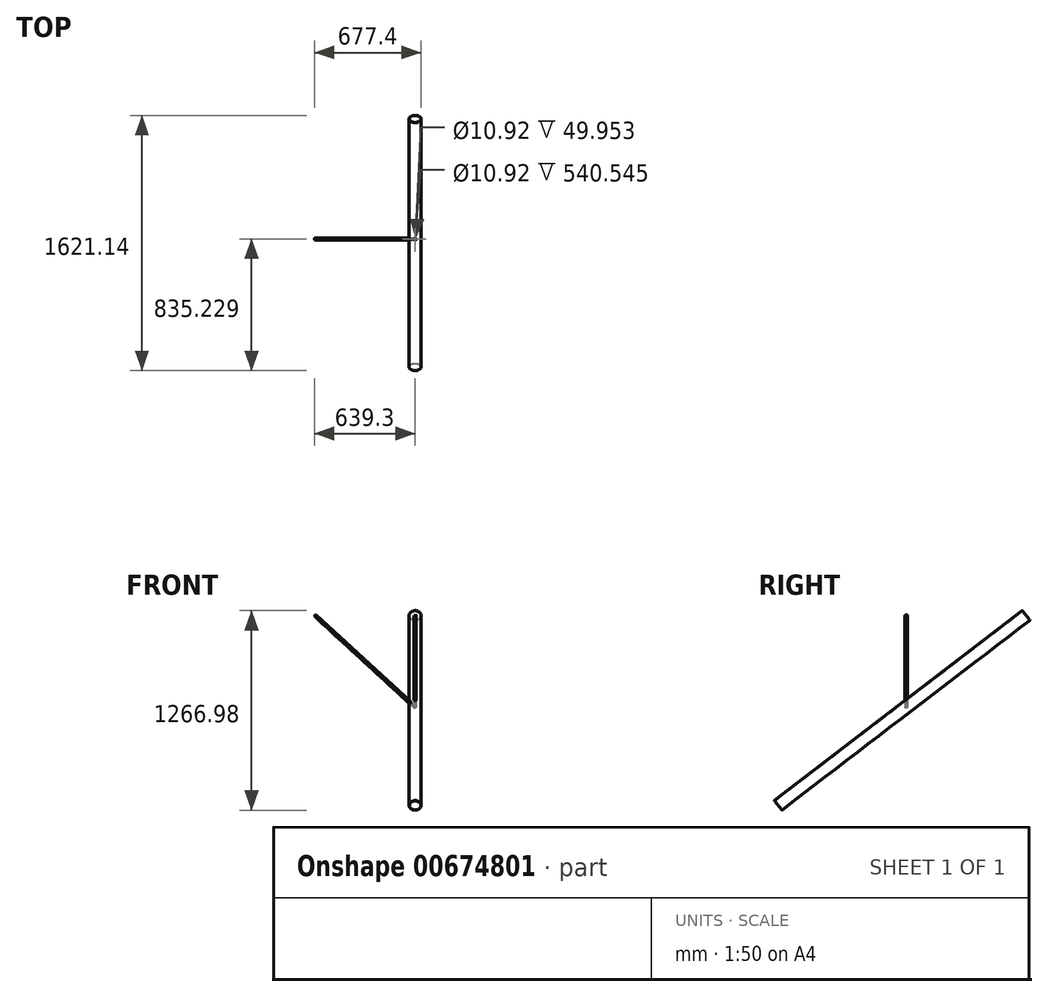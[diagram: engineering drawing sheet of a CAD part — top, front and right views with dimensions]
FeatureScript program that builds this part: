
annotation { "Feature Type Name" : "Feature", "Feature Type Description" : "" }
export const myFeature = defineFeature(function(context is Context, id is Id, definition is map)
    precondition{}
    {
        {
            var Q0;
            Q0=qCreatedBy(makeId("Right.planeOp"),FACE);
            var sketch = newSketch(context, id + "F0", { "sketchPlane" : qUnion([Q0])});
            skLineSegment(sketch, "E0", {"start": v(0, 0) * mm, "end": v(-1574.8, -1206.5) * mm});
            skSolve(sketch);
        }
        {
            var Q0;
            Q0=sQuery(id+"F0.wireOp",VERTEX,"E0.end");
            var Q1;
            Q1=sQuery(id+"F0.wireOp",EDGE,"E0");
            cPlane(context, id + "F1", {"entities" : qUnion([Q0, Q1]), "cplaneType" : CPlaneType.LINE_POINT, "offset" : 25.4 * mm, "width" : 152.4 * mm, "height" : 152.4 * mm});
        }
        {
            var Q0;
            Q0=qCreatedBy(id+"F1.planeOp",FACE);
            var sketch = newSketch(context, id + "F2", { "sketchPlane" : qUnion([Q0])});
            skCircle(sketch, "E1", {"center": v(0, 0) * mm, "radius": 38.1 * mm});
            skSolve(sketch);
        }
        {
            var Q0;
            Q0=makeQuery(id+"F2.imprint","IMPRINT",FACE,{"disambiguationData":[TD([[makeQuery(id+"F2.imprint","IMPRINT",EDGE,{"derivedFrom":sQuery(id+"F2.wireOp",EDGE,"E1")}),1.0]])]});
            var Q1;
            Q1=sQuery(id+"F0.wireOp",EDGE,"E0");
            sweep(context, id + "F3", {"profiles" : qUnion([Q0]), "path" : qUnion([Q1])});
        }
        {
            var Q0;
            Q0=qCreatedBy(id+"F1.planeOp",FACE);
            var sketch = newSketch(context, id + "F4", { "sketchPlane" : qUnion([Q0])});
            skCircle(sketch, "E2", {"center": v(0, 0) * mm, "radius": 36.45 * mm});
            skSolve(sketch);
        }
        {
            var Q0;
            Q0 = qSketchRegion(id + "F4", true);
            var Q1;
            Q1 = qConstructionFilter(qBodyType(qCreatedBy(id + "F0" ,EDGE), BodyType.WIRE), ConstructionObject.NO);
            sweep(context, id + "F5", {"operationType" : NewBodyOperationType.REMOVE, "profiles" : qUnion([Q0]), "path" : qUnion([Q1])});
        }
        {
            var Q0;
            Q0=qCreatedBy(makeId("Right.planeOp"),FACE);
            var sketch = newSketch(context, id + "F6", { "sketchPlane" : qUnion([Q0])});
            skLineSegment(sketch, "E3", {"start": v(-762, 0) * mm, "end": v(-762, -584.2) * mm});
            skSolve(sketch);
        }
        {
            var Q0;
            Q0=sQuery(id+"F6.wireOp",VERTEX,"E3.start");
            var Q1;
            Q1=sQuery(id+"F6.wireOp",EDGE,"E3");
            cPlane(context, id + "F7", {"entities" : qUnion([Q0, Q1]), "cplaneType" : CPlaneType.LINE_POINT, "offset" : 25.4 * mm, "width" : 152.4 * mm, "height" : 152.4 * mm});
        }
        {
            var Q0;
            Q0=qCreatedBy(id+"F7.planeOp",FACE);
            var sketch = newSketch(context, id + "F8", { "sketchPlane" : qUnion([Q0])});
            skCircle(sketch, "E4", {"center": v(0, 762.74) * mm, "radius": 6.35 * mm});
            skCircle(sketch, "E5", {"center": v(0, 762.74) * mm, "radius": 5.46 * mm});
            skSolve(sketch);
        }
        {
            var Q0;
            Q0=makeQuery(id+"F8.imprint","IMPRINT",FACE,{"disambiguationData":[TD([[makeQuery(id+"F8.imprint","IMPRINT",EDGE,{"derivedFrom":sQuery(id+"F8.wireOp",EDGE,"E4")}),1.0]])]});
            var Q1;
            Q1=sQuery(id+"F6.wireOp",EDGE,"E3");
            sweep(context, id + "F9", {"operationType" : NewBodyOperationType.ADD, "profiles" : qUnion([Q0]), "path" : qUnion([Q1])});
        }
        {
            var Q0;
            Q0=qCreatedBy(id+"F7.planeOp",FACE);
            var sketch = newSketch(context, id + "F10", { "sketchPlane" : qUnion([Q0])});
            skPoint(sketch, "E6", {"position": v(0, 761.82) * mm});
            skSolve(sketch);
        }
        {
            var Q0;
            Q0=qCreatedBy(id+"F7.planeOp",FACE);
            var sketch = newSketch(context, id + "F11", { "sketchPlane" : qUnion([Q0])});
            skLineSegment(sketch, "E7", {"start": v(0, 761.82) * mm, "end": v(0, 507.82) * mm, "construction": true});
            skSolve(sketch);
        }
        {
            var Q0;
            Q0=sQuery(id+"F10.wireOp",VERTEX,"E6");
            var Q1;
            Q1=sQuery(id+"F11.wireOp",EDGE,"E7");
            cPlane(context, id + "F12", {"entities" : qUnion([Q0, Q1]), "cplaneType" : CPlaneType.LINE_POINT, "offset" : 25.4 * mm, "width" : 152.4 * mm, "height" : 152.4 * mm});
        }
        {
            var Q0;
            Q0=qCreatedBy(id+"F12.planeOp",FACE);
            var sketch = newSketch(context, id + "F13", { "sketchPlane" : qUnion([Q0])});
            skLineSegment(sketch, "E8", {"start": v(0, -584.2) * mm, "end": v(635, 0) * mm});
            skSolve(sketch);
        }
        {
            var Q0;
            Q0=sQuery(id+"F13.wireOp",VERTEX,"E8.end");
            var Q1;
            Q1=sQuery(id+"F13.wireOp",EDGE,"E8");
            cPlane(context, id + "F14", {"entities" : qUnion([Q0, Q1]), "cplaneType" : CPlaneType.LINE_POINT, "offset" : 25.4 * mm, "width" : 152.4 * mm, "height" : 152.4 * mm});
        }
        {
            var Q0;
            Q0=qCreatedBy(id+"F14.planeOp",FACE);
            var sketch = newSketch(context, id + "F15", { "sketchPlane" : qUnion([Q0])});
            skCircle(sketch, "E9", {"center": v(761.82, -429.93) * mm, "radius": 6.35 * mm});
            skCircle(sketch, "E10", {"center": v(761.82, -429.93) * mm, "radius": 5.46 * mm});
            skSolve(sketch);
        }
        {
            var Q0;
            Q0=makeQuery(id+"F15.imprint","IMPRINT",FACE,{"disambiguationData":[TD([[makeQuery(id+"F15.imprint","IMPRINT",EDGE,{"derivedFrom":sQuery(id+"F15.wireOp",EDGE,"E9")}),1.0]])]});
            var Q1;
            Q1=sQuery(id+"F13.wireOp",EDGE,"E8");
            sweep(context, id + "F16", {"operationType" : NewBodyOperationType.ADD, "profiles" : qUnion([Q0]), "path" : qUnion([Q1])});
        }
    });
